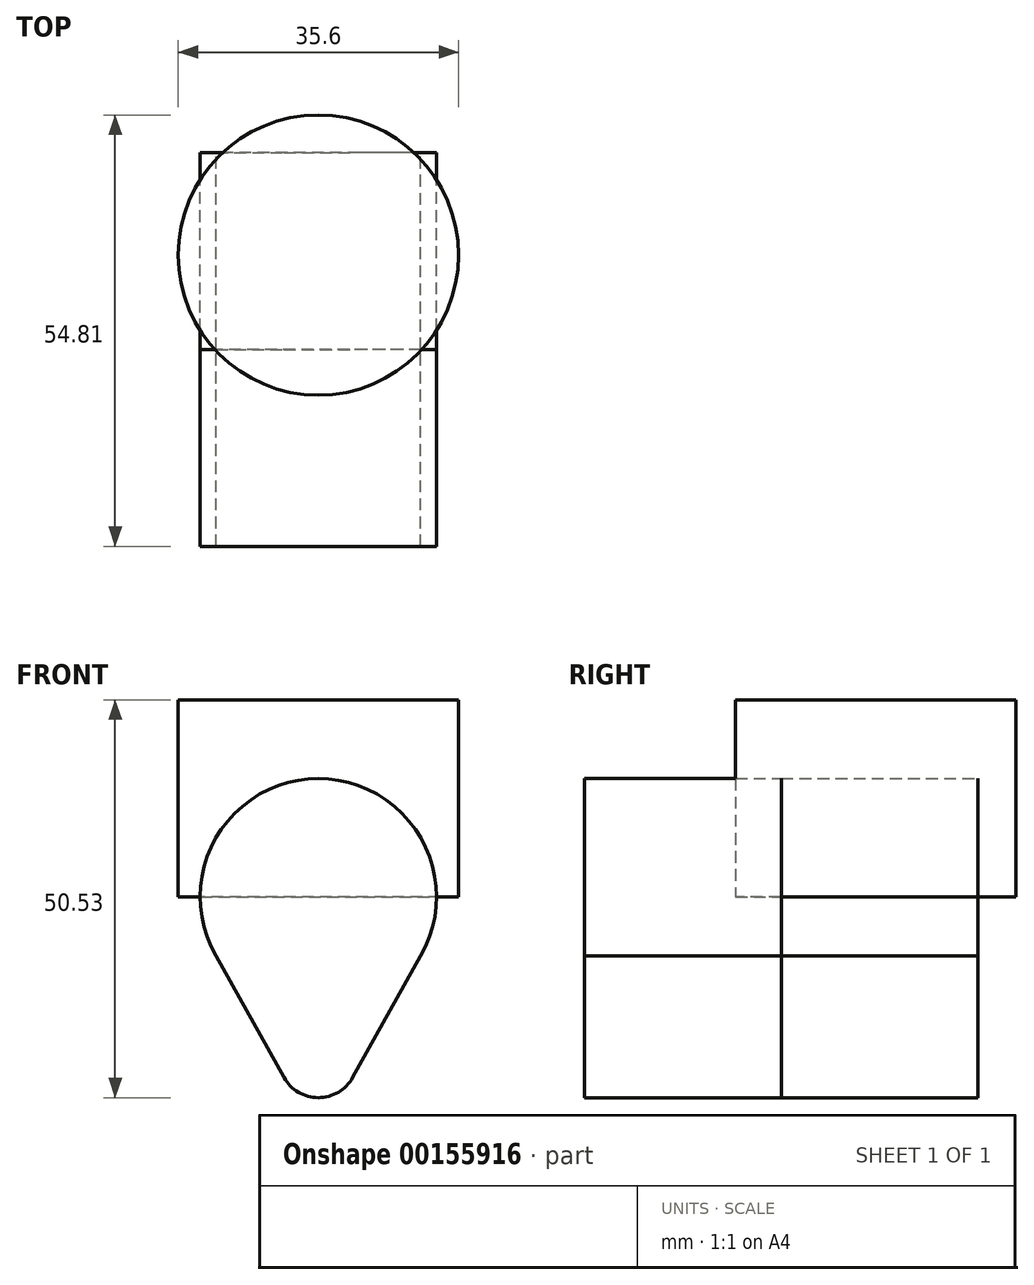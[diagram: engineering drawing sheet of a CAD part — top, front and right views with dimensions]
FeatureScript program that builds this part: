
annotation { "Feature Type Name" : "Feature", "Feature Type Description" : "" }
export const myFeature = defineFeature(function(context is Context, id is Id, definition is map)
    precondition{}
    {
        {
            var Q0;
            Q0=qCreatedBy(makeId("Front.planeOp"),FACE);
            var sketch = newSketch(context, id + "F0", { "sketchPlane" : qUnion([Q0])});
            skArc(sketch, "E0", {"start": v(12.99, -7.5) * mm, "mid": v(0, 15) * mm, "end": v(-12.99, -7.5) * mm});
            skArc(sketch, "E1", {"start": v(-4.37, -22.97) * mm, "mid": v(0, -25.53) * mm, "end": v(4.37, -22.97) * mm});
            skLineSegment(sketch, "E2", {"start": v(0, 0) * mm, "end": v(0, -20.53) * mm, "construction": true});
            skLineSegment(sketch, "E3", {"start": v(-12.99, -7.5) * mm, "end": v(-4.37, -22.97) * mm});
            skLineSegment(sketch, "E4", {"start": v(12.99, -7.5) * mm, "end": v(4.37, -22.97) * mm});
            skSolve(sketch);
        }
        {
            var Q0;
            {var subQ0=sQuery(id+"F0.wireOp",EDGE,"E0");var subQ1=makeQuery(id+"F0.imprint","INTERSECT",VERTEX,{"derivedFrom":[subQ0,sQuery(id+"F0.wireOp",EDGE,"E3")]});Q0=makeQuery(id+"F0.imprint","IMPRINT",FACE,{"disambiguationData":[TD([[makeQuery(id+"F0.imprint","IMPRINT",EDGE,{"disambiguationData":[TD([[subQ1,-1.0]])],"derivedFrom":subQ0}),1.0]])]});}
            var Q1;
            {var subQ0=sQuery(id+"F0.wireOp",EDGE,"E3");Q1=makeQuery(id+"F0.imprint","IMPRINT",FACE,{"disambiguationData":[TD([[makeQuery(id+"F0.imprint","IMPRINT",EDGE,{"derivedFrom":subQ0}),1.0]])]});}
            var Q2;
            {var subQ0=sQuery(id+"F0.wireOp",EDGE,"E1");var subQ1=makeQuery(id+"F0.imprint","INTERSECT",VERTEX,{"derivedFrom":[subQ0,sQuery(id+"F0.wireOp",EDGE,"E3")]});Q2=makeQuery(id+"F0.imprint","IMPRINT",FACE,{"disambiguationData":[TD([[makeQuery(id+"F0.imprint","IMPRINT",EDGE,{"disambiguationData":[TD([[subQ1,-1.0]])],"derivedFrom":subQ0}),1.0]])]});}
            extrude(context, id + "F1", {"entities" : qUnion([Q0, Q1, Q2]), "depth" : 25 * mm});
        }
        {
            var Q0;
            Q0=qCreatedBy(makeId("Top.planeOp"),FACE);
            var sketch = newSketch(context, id + "F2", { "sketchPlane" : qUnion([Q0])});
            skCircle(sketch, "E5", {"center": v(0, -12.99) * mm, "radius": 17.8 * mm});
            skSolve(sketch);
        }
        {
            var Q0;
            Q0 = qSketchRegion(id + "F2", true);
            extrude(context, id + "F3", {"entities" : qUnion([Q0]), "depth" : 25 * mm});
        }
        {
            var Q0;
            Q0=makeQuery(id+"F1.opExtrude","CAP_FACE",FACE,{"disambiguationData":[OSD([sQuery(id+"F0.wireOp",EDGE,"E0"),sQuery(id+"F0.wireOp",EDGE,"E1"),sQuery(id+"F0.wireOp",EDGE,"E3"),sQuery(id+"F0.wireOp",EDGE,"E4")])],"isStart":false});
            var sketch = newSketch(context, id + "F4", { "sketchPlane" : qUnion([Q0])});
            skArc(sketch, "E6.0", {"start": v(12.99, -7.5) * mm, "mid": v(0, 15) * mm, "end": v(-12.99, -7.5) * mm});
            skLineSegment(sketch, "E7.0", {"start": v(-12.99, -7.5) * mm, "end": v(-4.37, -22.97) * mm});
            skArc(sketch, "E8.0", {"start": v(-4.37, -22.97) * mm, "mid": v(0, -25.53) * mm, "end": v(4.37, -22.97) * mm});
            skLineSegment(sketch, "E9.0", {"start": v(12.99, -7.5) * mm, "end": v(4.37, -22.97) * mm});
            skSolve(sketch);
        }
        {
            var Q0;
            Q0 = qSketchRegion(id + "F4", true);
            extrude(context, id + "F5", {"entities" : qUnion([Q0]), "depth" : 25 * mm});
        }
    });
